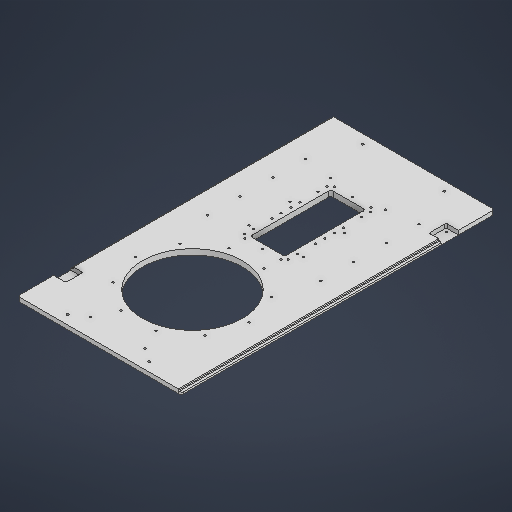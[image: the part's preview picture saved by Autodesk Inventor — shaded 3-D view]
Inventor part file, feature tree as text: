
AUTODESK INVENTOR PART (.ipt)
format: ipt  version: 2025 (Build 290162000, 162)  size: 481,792 bytes
history: native  units: in
note: dims shown in document units (in); Inventor stores cm internally (conversion verified against a paired STEP export)
features: sketch x16, extrude x5, hole x5, chamfer x4, fillet x3, plane x2
ambient origin geometry x8: Origin, YZ Plane, XZ Plane, XY Plane, X Axis, Y Axis, Z Axis, Center Point
bodies: Solid1 (feature_tree)
feature tree (35):
  extrude  "Extrusion1"  Depth=27.1654in
  sketch  "Sketch2"  dims[d5=8.6614in d6=0.0in d7=0.0in]
  extrude  "Extrusion2"  Depth=0.4724in
  plane  "Work Plane1"
  hole  "Hole3"  [1 undecoded]
  sketch  "Sketch7"  dims[d82=1.063in]
  plane  "Work Plane2"
  hole  "Hole4"  [1 undecoded]
  sketch  "Sketch9"  dims[d84=1.4961in]
  fillet  "Fillet2"  Radius=7.0625in
  extrude  "Extrusion7"  Depth=0.3937in
  extrude  "Extrusion8"  Depth=9.8425in
  chamfer  "Chamfer3"  Distance=3.937in Angle=360.0deg
  chamfer  "Chamfer4"  Distance=0.1181in
  hole  "Hole5"  [1 undecoded]
  chamfer  "Chamfer5"  Distance=0.3543in
  hole  "Hole6"  [1 undecoded]
  sketch  "Sketch15"  dims[d88=0.1969in d95=0.1181in d96=0.1181in d97=0.3543in d98=0.0in d99=0.2362in d100=0.2362in d101=0.122in d102=0.0in d103=0.0787in d104=0.1378in d105=45.0deg d106=0.0787in d107=0.1378in d108=45.0deg d110=0.315in d111=0.8661in d113=0.1299in d114=0.1299in d115=0.1299in d116=0.1299in d118=0.315in d119=0.8661in d122=0.1276in d123=0.315in d124=0.1575in d125=0.0787in d126=90.0deg d127=0.315in d128=0.8108in d129=0.0138in d130=0.0787in d131=45.0deg d146=3.9469in d147=0.7874in d148=0.3937in d149=0.1575in d150=3.937in d152=1.1811in d153=0.3937in d155=0.3937in d157=0.1575in d158=1.1811in d160=0.7874in d161=0.3937in d163=0.3937in d165=9.8425in d166=0.1575in d167=2.9528in d168=1.1811in d169=3.1496in d171=1.4173in d172=0.3937in d174=0.3937in d176=0.1628in d177=0.3937in d178=0.1575in d179=0.0787in d180=90.0deg d181=0.3937in d182=0.8108in d191=3.0in d192=7.0in d193=6.4961in d194=0.8312in d195=0.0in d196=0.1969in d197=0.3937in d198=0.1969in d199=1.9685in d201=0.7874in d202=0.3937in d204=0.3937in d206=0.3189in d207=0.1969in d208=0.3189in d209=1.9685in d211=0.7874in d212=0.3937in d214=0.3937in d216=0.1628in d217=0.3937in d218=0.1575in d219=0.0787in d220=90.0deg d221=0.3937in d222=0.8108in d232=0.1969in d233=0.1181in d234=0.0787in d235=45.0deg d26=0.0394in d27=0.0394in d28=0.0394in d29=0.0059in d30=0.0098in d31=0.0148in d32=0.5635in d33=0.0295in d34=0.8108in d35=0.0025in d36=0.0295in d37=0.0148in d66=0.0197in d67=0.0344in d230=0.0197in d231=0.0344in]
  extrude  "Extrusion11"  Depth=0.2362in
  fillet  "Fillet3"  Radius=0.122in
  hole  "Hole7"  [1 undecoded]
  fillet  "Fillet5"  Radius=0.1378in
  chamfer  "Chamfer6"  Distance=0.315in
  sketch  "Sketch1"  dims[d0=14.1732in d1=27.1654in]
  sketch  "Sketch6"  dims[d74=0.1628in d75=0.3937in d76=0.1575in d77=0.0787in d78=90.0deg d79=0.3937in d80=0.8108in]
  sketch  "Sketch8"  dims[d83=1.063in]
  sketch  "Sketch Circular Pattern4"  dims[d57=0.1936in d58=0.3937in d59=0.1575in d60=0.0787in d61=90.0deg d62=0.3937in d63=0.8108in d64=10.3543in]
  sketch  "Sketch10"  dims[d85=1.4961in]
  sketch  "Sketch11"  dims[d86=3.1102in]
  sketch  "Sketch12"  dims[d87=3.1102in]
  sketch  "Sketch Rectangular Pattern1"  dims[d2=0.4724in d3=0.0in d4=8.0709in]
  sketch  "Sketch Rectangular Pattern2"  dims[d8=10.6299in d50=5.9055in d55=7.0625in]
  sketch  "Sketch Rectangular Pattern3"  dims[d56=25.5906in]
  sketch  "Sketch Rectangular Pattern4"  dims[d65=10.6299in d68=9.8425in]
  sketch  "Sketch Rectangular Pattern5"  dims[d69=0.1575in d70=3.937in d72=360.0deg]
note: 5 required parameter values undecoded (feature->parameter linkage not recoverable at this tier; creation-order binding heuristic only, values carry confidence <= 0.55)
